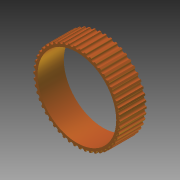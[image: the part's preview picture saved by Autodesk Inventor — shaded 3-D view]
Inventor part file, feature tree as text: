
AUTODESK INVENTOR PART (.ipt)
format: ipt  version: 2012 (Build 160160000, 160)  size: 280,576 bytes
history: native  units: in
note: dims shown in document units (in); Inventor stores cm internally (conversion verified against a paired STEP export)
features: extrude x1, sketch x1
ambient origin geometry x8: Origin, YZ Plane, XZ Plane, XY Plane, X Axis, Y Axis, Z Axis, Center Point
bodies: Solid1 (feature_tree)
feature tree (2):
  extrude  "Extrusion1"  Depth=1.45in
  sketch  "Sketch1"  dims[d0=2.625in d1=1.45in d3=19.685in d5=360.0deg d10=2.9in d11=0.875in d12=0.0in d17=0.0625in]
